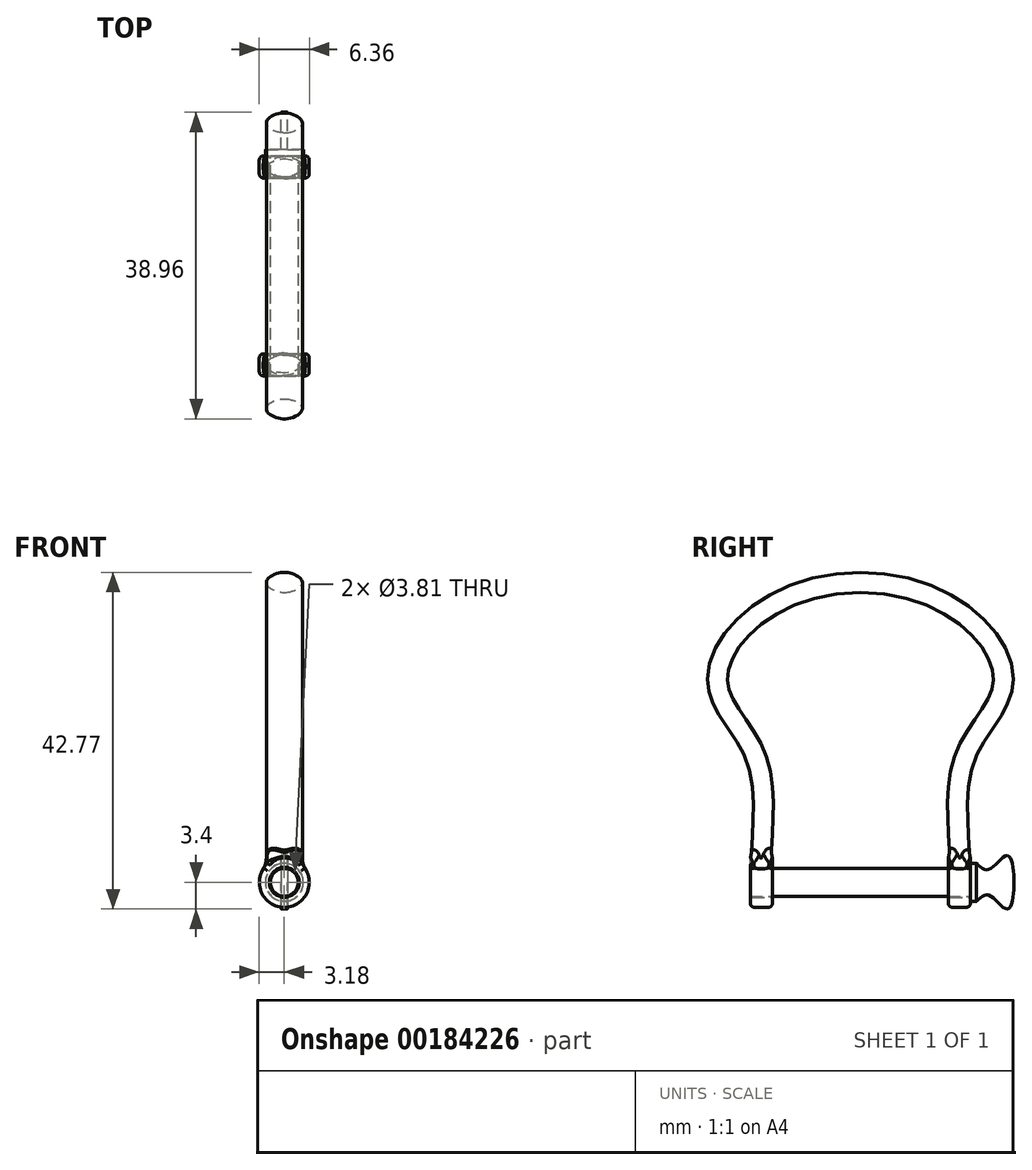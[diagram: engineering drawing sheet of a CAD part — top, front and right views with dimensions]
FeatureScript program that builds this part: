
annotation { "Feature Type Name" : "Feature", "Feature Type Description" : "" }
export const myFeature = defineFeature(function(context is Context, id is Id, definition is map)
    precondition{}
    {
        {
            var Q0;
            Q0=qCreatedBy(makeId("Right.planeOp"),FACE);
            var sketch = newSketch(context, id + "F0", { "sketchPlane" : qUnion([Q0])});
            skFitSpline(sketch, "E0", {"points": [v(-12.7, 0) * mm, v(-13.34, 16.07) * mm, v(-18.16, 26.12) * mm, v(0, 38.1) * mm], "startDerivative": vector(0, 52.63) * mm, "endDerivative": vector(82.9, 0) * mm});
            skLineSegment(sketch, "E1", {"start": v(0, 0) * mm, "end": v(0, 38.1) * mm, "construction": true});
            skFitSpline(sketch, "E2.0.MirrorCS", {"points": [v(12.7, 0) * mm, v(13.34, 16.07) * mm, v(18.16, 26.12) * mm, v(0, 38.1) * mm], "startDerivative": vector(0, 52.63) * mm, "endDerivative": vector(-82.9, 0) * mm});
            skSolve(sketch);
        }
        {
            var Q0;
            Q0=qCreatedBy(makeId("Top.planeOp"),FACE);
            var sketch = newSketch(context, id + "F1", { "sketchPlane" : qUnion([Q0])});
            skLineSegment(sketch, "E3", {"start": v(0, 12.7) * mm, "end": v(0, 13.97) * mm, "construction": true});
            skLineSegment(sketch, "E4", {"start": v(0, 12.7) * mm, "end": v(0, 11.43) * mm, "construction": true});
            skLineSegment(sketch, "E5", {"start": v(0, 12.7) * mm, "end": v(2.29, 12.7) * mm, "construction": true});
            skLineSegment(sketch, "E6", {"start": v(0, 12.7) * mm, "end": v(-2.29, 12.7) * mm, "construction": true});
            skFitSpline(sketch, "E7", {"points": [v(0, 11.43) * mm, v(2.29, 12.7) * mm, v(0, 13.97) * mm, v(-2.29, 12.7) * mm, v(0, 11.43) * mm]});
            skSolve(sketch);
        }
        {
            var Q0;
            Q0=makeQuery(id+"F1.imprint","IMPRINT",FACE,{"disambiguationData":[TD([[makeQuery(id+"F1.imprint","IMPRINT",EDGE,{"derivedFrom":sQuery(id+"F1.wireOp",EDGE,"E7")}),1.0]])]});
            var Q1;
            Q1=sQuery(id+"F0.wireOp",EDGE,"E2.0.MirrorCS");
            var Q2;
            Q2=sQuery(id+"F0.wireOp",EDGE,"E0");
            sweep(context, id + "F2", {"profiles" : qUnion([Q0]), "path" : qUnion([Q1, Q2])});
        }
        {
            var Q0;
            Q0=qCreatedBy(makeId("Top.planeOp"),FACE);
            var sketch = newSketch(context, id + "F3", { "sketchPlane" : qUnion([Q0])});
            skFitSpline(sketch, "E8.0", {"points": [v(0, -11.43) * mm, v(1.14, -11.43) * mm, v(3.43, -12.7) * mm, v(0, -14.6) * mm, v(-3.43, -12.7) * mm, v(-1.14, -11.43) * mm, v(0, -11.43) * mm], "construction": true});
            skLineSegment(sketch, "E9", {"start": v(0, -13.97) * mm, "end": v(0, -11.43) * mm});
            skSolve(sketch);
        }
        {
            var Q0;
            Q0=sQuery(id+"F3.wireOp",VERTEX,"E9.start");
            var Q1;
            Q1=sQuery(id+"F3.wireOp",EDGE,"E9");
            cPlane(context, id + "F4", {"entities" : qUnion([Q0, Q1]), "cplaneType" : CPlaneType.CURVE_POINT, "offset" : 152.4 * mm, "width" : 152.4 * mm, "height" : 152.4 * mm});
        }
        {
            var Q0;
            Q0=qCreatedBy(id+"F4.planeOp",FACE);
            var sketch = newSketch(context, id + "F5", { "sketchPlane" : qUnion([Q0])});
            skCircle(sketch, "E10", {"center": v(0, 0) * mm, "radius": 3.18 * mm});
            skSolve(sketch);
        }
        {
            var Q0;
            Q0=makeQuery(id+"F5.imprint","IMPRINT",FACE,{"disambiguationData":[TD([[makeQuery(id+"F5.imprint","IMPRINT",EDGE,{"derivedFrom":sQuery(id+"F5.wireOp",EDGE,"E10")}),1.0]])]});
            var Q1;
            Q1=makeQuery(id+"F2.opSweep","SWEPT_FACE",FACE,{"disambiguationData":[OSD([sQuery(id+"F0.wireOp",EDGE,"E2.0.MirrorCS"),sQuery(id+"F1.wireOp",EDGE,"E7")])]});
            extrude(context, id + "F6", {"entities" : qUnion([Q0]), "endBoundEntity" : qUnion([Q1]), "depth" : 2.8 * mm});
        }
        {
            var Q0;
            Q0=makeQuery(id+"F6.opExtrude","SWEPT_BODY",BODY,{"disambiguationData":[OSD([sQuery(id+"F5.wireOp",EDGE,"E10")])]});
            var Q1;
            Q1=qCreatedBy(makeId("Front.planeOp"),FACE);
            mirror(context, id + "F7", {"entities" : qUnion([Q0]), "mirrorPlane" : qUnion([Q1])});
        }
        {
            var Q0;
            Q0=makeQuery(id+"F7.opPattern","COPY",BODY,{"derivedFrom":makeQuery(id+"F6.opExtrude","SWEPT_BODY",BODY,{"disambiguationData":[OSD([sQuery(id+"F5.wireOp",EDGE,"E10")])]}),"instanceName":"1"});
            var Q1;
            Q1=makeQuery(id+"F2.opSweep","SWEPT_BODY",BODY,{"disambiguationData":[OSD([sQuery(id+"F0.wireOp",EDGE,"E0"),sQuery(id+"F1.wireOp",EDGE,"E7")])]});
            var Q2;
            Q2=makeQuery(id+"F6.opExtrude","SWEPT_BODY",BODY,{"disambiguationData":[OSD([sQuery(id+"F5.wireOp",EDGE,"E10")])]});
            booleanBodies(context, id + "F8", {"operationType" : BooleanOperationType.UNION, "tools" : qUnion([Q0, Q1, Q2])});
        }
        {
            var Q0;
            Q0=makeQuery(id+"F8.opBoolean","INTERSECT",EDGE,{"derivedFrom":[makeQuery(id+"F2.opSweep","SWEPT_FACE",FACE,{"disambiguationData":[OSD([sQuery(id+"F0.wireOp",EDGE,"E0"),sQuery(id+"F1.wireOp",EDGE,"E7")])]}),makeQuery(id+"F6.opExtrude","SWEPT_FACE",FACE,{"disambiguationData":[OSD([sQuery(id+"F5.wireOp",EDGE,"E10")])]})]});
            var Q1;
            Q1=makeQuery(id+"F8.opBoolean","INTERSECT",EDGE,{"derivedFrom":[makeQuery(id+"F2.opSweep","SWEPT_FACE",FACE,{"disambiguationData":[OSD([sQuery(id+"F0.wireOp",EDGE,"E2.0.MirrorCS"),sQuery(id+"F1.wireOp",EDGE,"E7")])]}),makeQuery(id+"F7.opPattern","COPY",FACE,{"derivedFrom":makeQuery(id+"F6.opExtrude","SWEPT_FACE",FACE,{"disambiguationData":[OSD([sQuery(id+"F5.wireOp",EDGE,"E10")])]}),"instanceName":"1"})]});
            fillet(context, id + "F9", {"entities" : qUnion([Q0, Q1]), "radius" : 2.54 * mm, "tangentPropagation" : true, "allowEdgeOverflow" : false});
        }
        {
            var Q0;
            Q0=makeQuery(id+"F6.opExtrude","CAP_EDGE",EDGE,{"disambiguationData":[OSD([sQuery(id+"F5.wireOp",EDGE,"E10")])],"isStart":false});
            var Q1;
            Q1=makeQuery(id+"F6.opExtrude","CAP_EDGE",EDGE,{"disambiguationData":[OSD([sQuery(id+"F5.wireOp",EDGE,"E10")])],"isStart":true});
            var Q2;
            Q2=makeQuery(id+"F7.opPattern","COPY",EDGE,{"derivedFrom":makeQuery(id+"F6.opExtrude","CAP_EDGE",EDGE,{"disambiguationData":[OSD([sQuery(id+"F5.wireOp",EDGE,"E10")])],"isStart":false}),"instanceName":"1"});
            var Q3;
            Q3=makeQuery(id+"F7.opPattern","COPY",EDGE,{"derivedFrom":makeQuery(id+"F6.opExtrude","CAP_EDGE",EDGE,{"disambiguationData":[OSD([sQuery(id+"F5.wireOp",EDGE,"E10")])],"isStart":true}),"instanceName":"1"});
            var Q4;
            {var subQ0=sQuery(id+"F5.wireOp",EDGE,"E10");Q4=makeQuery(id+"F9.opFillet","BLEND_EDGE",EDGE,{"blendedFrom":[makeQuery(id+"F8.opBoolean","INTERSECT",EDGE,{"derivedFrom":[makeQuery(id+"F2.opSweep","SWEPT_FACE",FACE,{"disambiguationData":[OSD([sQuery(id+"F0.wireOp",EDGE,"E2.0.MirrorCS"),sQuery(id+"F1.wireOp",EDGE,"E7")])]}),makeQuery(id+"F7.opPattern","COPY",FACE,{"derivedFrom":makeQuery(id+"F6.opExtrude","SWEPT_FACE",FACE,{"disambiguationData":[OSD([subQ0])]}),"instanceName":"1"})]}),makeQuery(id+"F7.opPattern","COPY",FACE,{"derivedFrom":makeQuery(id+"F6.opExtrude","CAP_FACE",FACE,{"disambiguationData":[OSD([subQ0])],"isStart":false}),"instanceName":"1"})],"blendedInto":[makeQuery(id+"F7.opPattern","COPY",FACE,{"derivedFrom":makeQuery(id+"F6.opExtrude","CAP_FACE",FACE,{"disambiguationData":[OSD([subQ0])],"isStart":false}),"instanceName":"1"})]});}
            var Q5;
            {var subQ0=sQuery(id+"F5.wireOp",EDGE,"E10");Q5=makeQuery(id+"F9.opFillet","BLEND_EDGE",EDGE,{"blendedFrom":[makeQuery(id+"F8.opBoolean","INTERSECT",EDGE,{"derivedFrom":[makeQuery(id+"F2.opSweep","SWEPT_FACE",FACE,{"disambiguationData":[OSD([sQuery(id+"F0.wireOp",EDGE,"E2.0.MirrorCS"),sQuery(id+"F1.wireOp",EDGE,"E7")])]}),makeQuery(id+"F7.opPattern","COPY",FACE,{"derivedFrom":makeQuery(id+"F6.opExtrude","SWEPT_FACE",FACE,{"disambiguationData":[OSD([subQ0])]}),"instanceName":"1"})]}),makeQuery(id+"F7.opPattern","COPY",FACE,{"derivedFrom":makeQuery(id+"F6.opExtrude","CAP_FACE",FACE,{"disambiguationData":[OSD([subQ0])],"isStart":true}),"instanceName":"1"})],"blendedInto":[makeQuery(id+"F7.opPattern","COPY",FACE,{"derivedFrom":makeQuery(id+"F6.opExtrude","CAP_FACE",FACE,{"disambiguationData":[OSD([subQ0])],"isStart":true}),"instanceName":"1"})]});}
            var Q6;
            {var subQ0=sQuery(id+"F5.wireOp",EDGE,"E10");Q6=makeQuery(id+"F9.opFillet","BLEND_EDGE",EDGE,{"blendedFrom":[makeQuery(id+"F8.opBoolean","INTERSECT",EDGE,{"derivedFrom":[makeQuery(id+"F2.opSweep","SWEPT_FACE",FACE,{"disambiguationData":[OSD([sQuery(id+"F0.wireOp",EDGE,"E0"),sQuery(id+"F1.wireOp",EDGE,"E7")])]}),makeQuery(id+"F6.opExtrude","SWEPT_FACE",FACE,{"disambiguationData":[OSD([subQ0])]})]}),makeQuery(id+"F6.opExtrude","CAP_FACE",FACE,{"disambiguationData":[OSD([subQ0])],"isStart":false})],"blendedInto":[makeQuery(id+"F6.opExtrude","CAP_FACE",FACE,{"disambiguationData":[OSD([subQ0])],"isStart":false})]});}
            var Q7;
            {var subQ0=sQuery(id+"F5.wireOp",EDGE,"E10");Q7=makeQuery(id+"F9.opFillet","BLEND_EDGE",EDGE,{"blendedFrom":[makeQuery(id+"F8.opBoolean","INTERSECT",EDGE,{"derivedFrom":[makeQuery(id+"F2.opSweep","SWEPT_FACE",FACE,{"disambiguationData":[OSD([sQuery(id+"F0.wireOp",EDGE,"E0"),sQuery(id+"F1.wireOp",EDGE,"E7")])]}),makeQuery(id+"F6.opExtrude","SWEPT_FACE",FACE,{"disambiguationData":[OSD([subQ0])]})]}),makeQuery(id+"F6.opExtrude","CAP_FACE",FACE,{"disambiguationData":[OSD([subQ0])],"isStart":true})],"blendedInto":[makeQuery(id+"F6.opExtrude","CAP_FACE",FACE,{"disambiguationData":[OSD([subQ0])],"isStart":true})]});}
            fillet(context, id + "F10", {"entities" : qUnion([Q0, Q1, Q2, Q3, Q4, Q5, Q6, Q7]), "radius" : 0.5 * mm, "allowEdgeOverflow" : false});
        }
        {
            var Q0;
            Q0=makeQuery(id+"F7.opPattern","COPY",FACE,{"derivedFrom":makeQuery(id+"F6.opExtrude","CAP_FACE",FACE,{"disambiguationData":[OSD([sQuery(id+"F5.wireOp",EDGE,"E10")])],"isStart":true}),"instanceName":"1"});
            var sketch = newSketch(context, id + "F11", { "sketchPlane" : qUnion([Q0])});
            skCircle(sketch, "E11", {"center": v(0, 0) * mm, "radius": 1.9 * mm});
            skSolve(sketch);
        }
        {
            var Q0;
            Q0=makeQuery(id+"F11.imprint","IMPRINT",FACE,{"disambiguationData":[TD([[makeQuery(id+"F11.imprint","IMPRINT",EDGE,{"derivedFrom":sQuery(id+"F11.wireOp",EDGE,"E11")}),1.0]])]});
            extrude(context, id + "F12", {"entities" : qUnion([Q0]), "operationType" : NewBodyOperationType.REMOVE, "endBound" : BoundingType.THROUGH_ALL, "oppositeDirection" : true, "depth" : 25.4 * mm});
        }
        {
            var Q0;
            Q0=makeQuery(id+"F12.boolean.opBoolean","COPY",FACE,{"disambiguationData":[OD(0.0)],"derivedFrom":makeQuery(id+"F12.opExtrude","SWEPT_FACE",FACE,{"disambiguationData":[OSD([sQuery(id+"F11.wireOp",EDGE,"E11")])]})});
            var Q1;
            Q1=makeQuery(id+"F12.boolean.opBoolean","COPY",FACE,{"disambiguationData":[OD(1.0)],"derivedFrom":makeQuery(id+"F12.opExtrude","SWEPT_FACE",FACE,{"disambiguationData":[OSD([sQuery(id+"F11.wireOp",EDGE,"E11")])]})});
            fillet(context, id + "F13", {"entities" : qUnion([Q0, Q1]), "radius" : 0.25 * mm, "tangentPropagation" : true, "allowEdgeOverflow" : false});
        }
        {
            var Q0;
            Q0=qCreatedBy(makeId("Right.planeOp"),FACE);
            var sketch = newSketch(context, id + "F14", { "sketchPlane" : qUnion([Q0])});
            skLineSegment(sketch, "E12.0", {"start": v(13.72, -1.9) * mm, "end": v(13.72, 1.9) * mm, "construction": true});
            skLineSegment(sketch, "E13.0", {"start": v(13.97, -2.67) * mm, "end": v(13.97, 1.51) * mm, "construction": true});
            skLineSegment(sketch, "E14", {"start": v(13.72, -1.78) * mm, "end": v(13.97, -1.78) * mm});
            skLineSegment(sketch, "E15", {"start": v(13.97, -1.78) * mm, "end": v(13.97, -2.41) * mm});
            skLineSegment(sketch, "E16", {"start": v(13.97, -2.41) * mm, "end": v(14.76, -2.41) * mm});
            skLineSegment(sketch, "E17", {"start": v(14.76, -2.41) * mm, "end": v(14.76, 0) * mm});
            skLineSegment(sketch, "E18.0", {"start": v(-13.97, 2.16) * mm, "end": v(-13.97, -2.16) * mm, "construction": true});
            skLineSegment(sketch, "E19", {"start": v(14.76, 0) * mm, "end": v(-13.97, 0) * mm});
            skLineSegment(sketch, "E20", {"start": v(13.72, -1.78) * mm, "end": v(-13.97, -1.78) * mm});
            skLineSegment(sketch, "E21", {"start": v(-13.97, -1.78) * mm, "end": v(-13.97, 0) * mm});
            skSolve(sketch);
        }
        {
            var Q0;
            Q0=makeQuery(id+"F14.imprint","IMPRINT",FACE,{"disambiguationData":[TD([[makeQuery(id+"F14.imprint","IMPRINT",EDGE,{"derivedFrom":sQuery(id+"F14.wireOp",EDGE,"E15")}),1.0]])]});
            var Q1;
            Q1=sQuery(id+"F14.wireOp",EDGE,"E19");
            revolve(context, id + "F15", {"entities" : qUnion([Q0]), "axis" : qUnion([Q1]), "revolveType" : RevolveType.FULL});
        }
        {
            var Q0;
            Q0=qCreatedBy(makeId("Right.planeOp"),FACE);
            var sketch = newSketch(context, id + "F16", { "sketchPlane" : qUnion([Q0])});
            skLineSegment(sketch, "E22.0", {"start": v(14.76, 2.41) * mm, "end": v(14.76, -2.41) * mm});
            skLineSegment(sketch, "E23", {"start": v(14.76, 0) * mm, "end": v(19.52, 0) * mm, "construction": true});
            skFitSpline(sketch, "E24", {"points": [v(14.76, 2.41) * mm, v(16.27, 1.63) * mm, v(18.7, 3.4) * mm, v(19.52, 0) * mm], "startDerivative": vector(4.77, -4.46) * mm, "endDerivative": vector(0, -9.68) * mm});
            skFitSpline(sketch, "E25.0.MirrorCS", {"points": [v(14.76, -2.41) * mm, v(16.27, -1.63) * mm, v(18.7, -3.4) * mm, v(19.52, 0) * mm], "startDerivative": vector(4.77, 4.46) * mm, "endDerivative": vector(0, 9.68) * mm});
            skSolve(sketch);
        }
        {
            var Q0;
            Q0=makeQuery(id+"F16.imprint","IMPRINT",FACE,{"disambiguationData":[TD([[makeQuery(id+"F16.imprint","IMPRINT",EDGE,{"derivedFrom":sQuery(id+"F16.wireOp",EDGE,"E22.0")}),1.0]])]});
            extrude(context, id + "F17", {"entities" : qUnion([Q0]), "operationType" : NewBodyOperationType.ADD, "endBound" : BoundingType.SYMMETRIC, "depth" : 0.76 * mm});
        }
        {
            var Q0;
            Q0=makeQuery(id+"F17.opExtrude","CAP_FACE",FACE,{"disambiguationData":[OSD([sQuery(id+"F16.wireOp",EDGE,"E22.0"),sQuery(id+"F16.wireOp",EDGE,"E24"),sQuery(id+"F16.wireOp",EDGE,"E25.0.MirrorCS")])],"isStart":false});
            var sketch = newSketch(context, id + "F18", { "sketchPlane" : qUnion([Q0])});
            skLineSegment(sketch, "E26.bottom", {"start": v(14.76, -2.38) * mm, "end": v(15, -2.38) * mm});
            skLineSegment(sketch, "E26.top", {"start": v(14.76, -2.55) * mm, "end": v(15, -2.55) * mm});
            skLineSegment(sketch, "E26.left", {"start": v(14.76, -2.38) * mm, "end": v(14.76, -2.55) * mm});
            skLineSegment(sketch, "E26.right", {"start": v(15, -2.38) * mm, "end": v(15, -2.55) * mm});
            skLineSegment(sketch, "E27.0", {"start": v(14.76, 2.38) * mm, "end": v(14.76, -2.38) * mm});
            skSolve(sketch);
        }
        {
            var Q0;
            {var subQ0=makeQuery(id+"F17.opExtrude","CAP_EDGE",EDGE,{"disambiguationData":[OSD([sQuery(id+"F16.wireOp",EDGE,"E25.0.MirrorCS")])],"isStart":false});var subQ3=sQuery(id+"F18.wireOp",EDGE,"E26.left");var subQ4=makeQuery(id+"F18.imprint","INTERSECT",VERTEX,{"derivedFrom":[subQ0,subQ3]});Q0=makeQuery(id+"F18.imprint","IMPRINT",FACE,{"disambiguationData":[TD([[makeQuery(id+"F18.imprint","IMPRINT",EDGE,{"disambiguationData":[TD([[subQ4,-1.0]])],"derivedFrom":subQ0}),1.0]])]});}
            var Q1;
            Q1=makeQuery(id+"F15.opRevolve","SWEPT_FACE",FACE,{"disambiguationData":[OSD([sQuery(id+"F14.wireOp",EDGE,"E16")])]});
            revolve(context, id + "F19", {"operationType" : NewBodyOperationType.REMOVE, "entities" : qUnion([Q0]), "axis" : qUnion([Q1]), "revolveType" : RevolveType.FULL, "oppositeDirection" : true});
        }
    });
